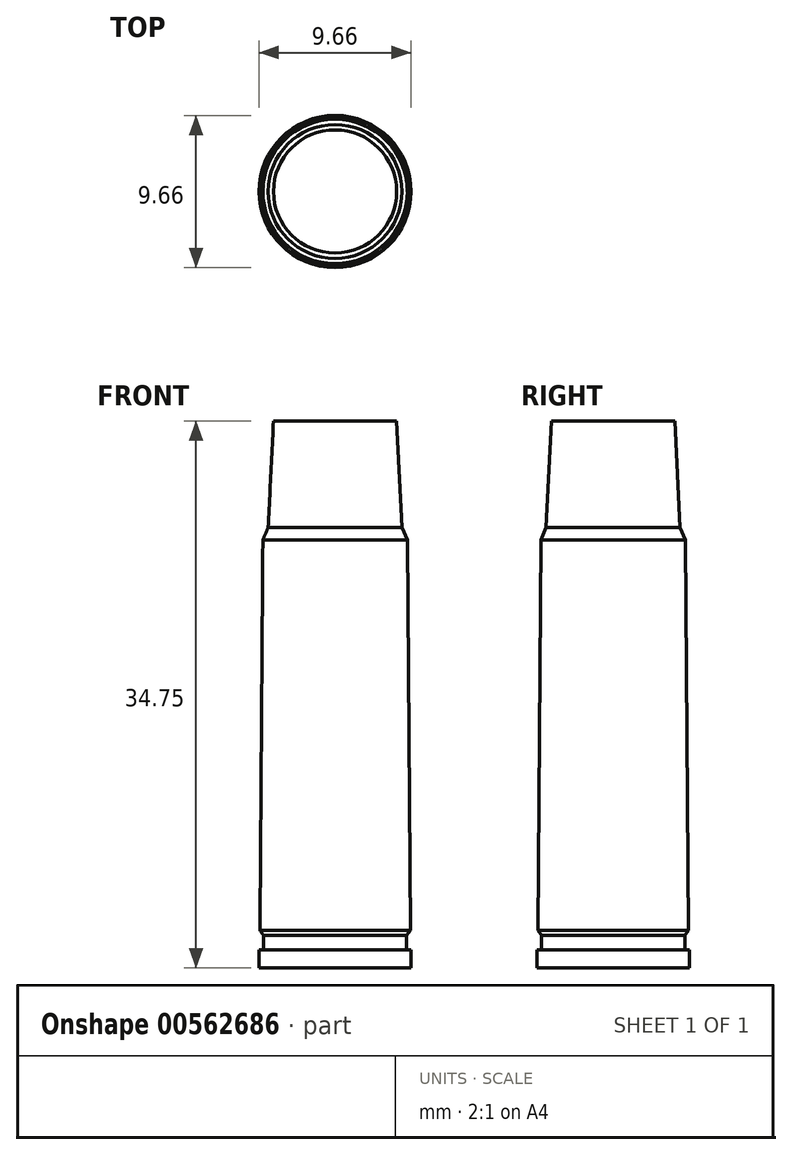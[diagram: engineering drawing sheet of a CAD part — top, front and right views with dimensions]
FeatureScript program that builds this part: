
annotation { "Feature Type Name" : "Feature", "Feature Type Description" : "" }
export const myFeature = defineFeature(function(context is Context, id is Id, definition is map)
    precondition{}
    {
        {
            var Q0;
            Q0=qCreatedBy(makeId("Front.planeOp"),FACE);
            var sketch = newSketch(context, id + "F0", { "sketchPlane" : qUnion([Q0])});
            skLineSegment(sketch, "E0", {"start": v(0, 0) * mm, "end": v(4.83, 0) * mm});
            skLineSegment(sketch, "E1", {"start": v(4.83, 0) * mm, "end": v(4.83, 1.14) * mm});
            skLineSegment(sketch, "E2", {"start": v(4.83, 1.14) * mm, "end": v(4.55, 1.14) * mm});
            skLineSegment(sketch, "E3", {"start": v(4.55, 1.14) * mm, "end": v(4.55, 2.08) * mm});
            skLineSegment(sketch, "E4", {"start": v(4.58, 27.2) * mm, "end": v(4.25, 28) * mm});
            skLineSegment(sketch, "E5", {"start": v(4.25, 28) * mm, "end": v(3.91, 34.75) * mm});
            skLineSegment(sketch, "E6", {"start": v(3.91, 34.75) * mm, "end": v(0, 34.75) * mm});
            skLineSegment(sketch, "E7", {"start": v(4.55, 2.08) * mm, "end": v(4.78, 2.4) * mm});
            skLineSegment(sketch, "E8", {"start": v(4.78, 2.4) * mm, "end": v(4.58, 27.2) * mm});
            skLineSegment(sketch, "E9", {"start": v(0, 34.75) * mm, "end": v(0, 0) * mm});
            skLineSegment(sketch, "E10", {"start": v(0, 44.91) * mm, "end": v(0, -14.84) * mm, "construction": true});
            skSolve(sketch);
        }
        {
            var Q0;
            Q0=sQuery(id+"F0.wireOp",EDGE,"E8");
            var Q1;
            Q1=sQuery(id+"F0.wireOp",EDGE,"E0");
            var Q2;
            Q2=sQuery(id+"F0.wireOp",EDGE,"E6");
            var Q3;
            Q3=sQuery(id+"F0.wireOp",EDGE,"E5");
            var Q4;
            Q4=sQuery(id+"F0.wireOp",EDGE,"E4");
            var Q5;
            Q5=sQuery(id+"F0.wireOp",EDGE,"E3");
            var Q6;
            Q6=sQuery(id+"F0.wireOp",EDGE,"E1");
            var Q7;
            Q7=sQuery(id+"F0.wireOp",EDGE,"E7");
            var Q8;
            Q8=sQuery(id+"F0.wireOp",EDGE,"E2");
            var Q9;
            Q9=sQuery(id+"F0.wireOp",EDGE,"E10");
            revolve(context, id + "F1", {"bodyType" : ToolBodyType.SURFACE, "surfaceEntities" : qUnion([Q0, Q1, Q2, Q3, Q4, Q5, Q6, Q7, Q8]), "axis" : qUnion([Q9]), "revolveType" : RevolveType.FULL});
        }
    });
